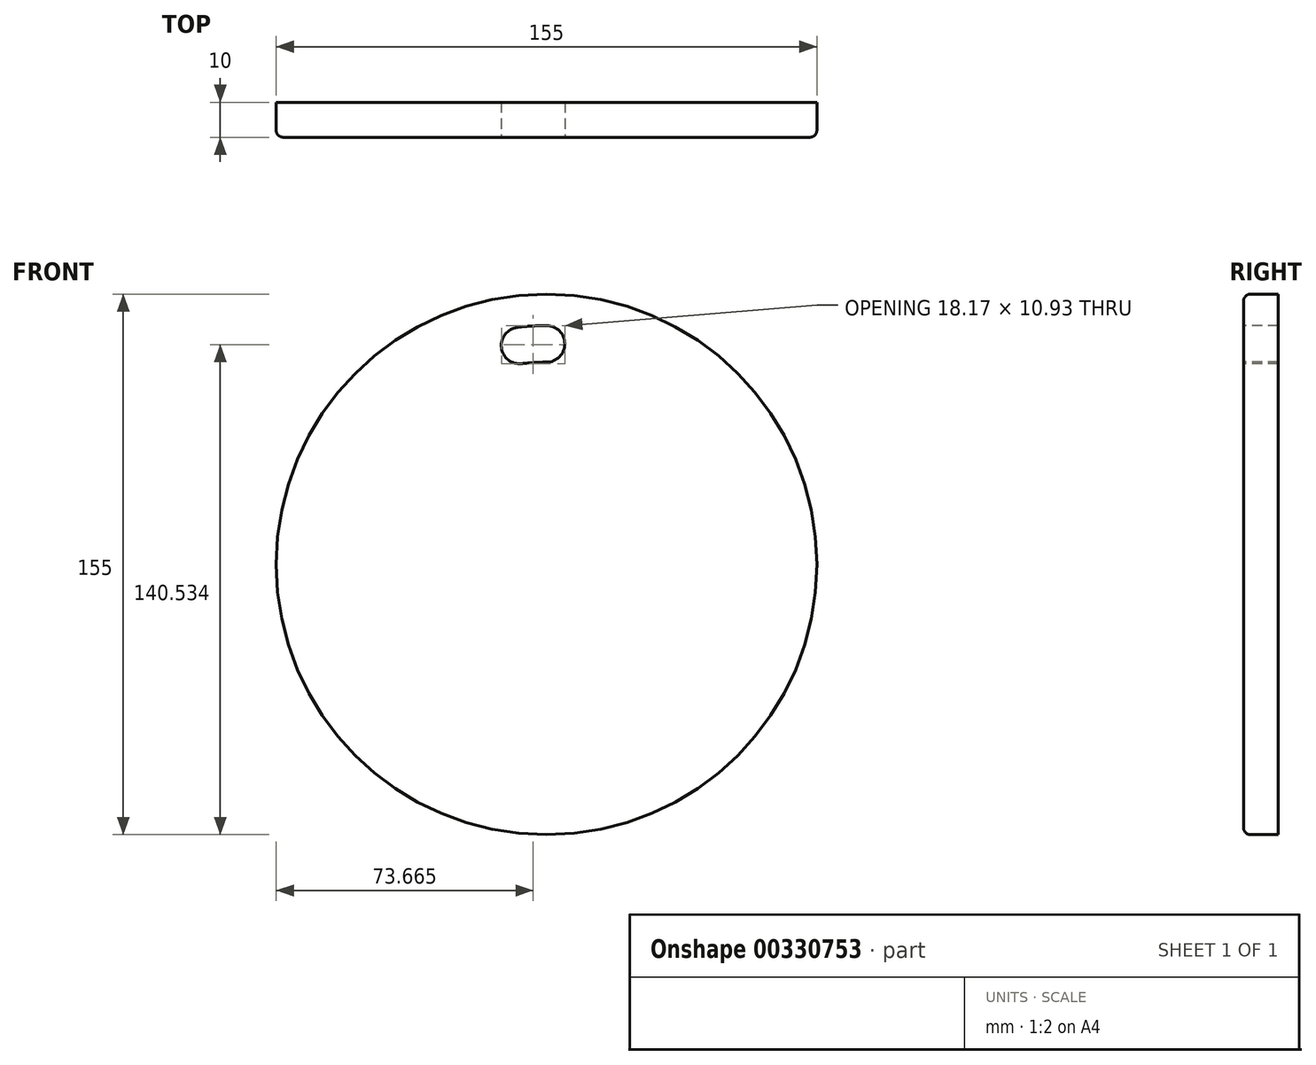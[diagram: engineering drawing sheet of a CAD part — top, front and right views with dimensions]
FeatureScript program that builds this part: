
annotation { "Feature Type Name" : "Feature", "Feature Type Description" : "" }
export const myFeature = defineFeature(function(context is Context, id is Id, definition is map)
    precondition{}
    {
        {
            var Q0;
            Q0=qCreatedBy(makeId("Front.planeOp"),FACE);
            var sketch = newSketch(context, id + "F0", { "sketchPlane" : qUnion([Q0])});
            skCircle(sketch, "E0", {"center": v(0, 0) * mm, "radius": 58 * mm, "construction": true});
            skCircle(sketch, "E1", {"center": v(0, 0) * mm, "radius": 68.5 * mm, "construction": true});
            skLineSegment(sketch, "E2", {"start": v(0, 63.25) * mm, "end": v(0, 58) * mm, "construction": true});
            skLineSegment(sketch, "E3", {"start": v(0, 68.5) * mm, "end": v(0, 63.25) * mm, "construction": true});
            skCircle(sketch, "E4", {"center": v(0, 0) * mm, "radius": 63.25 * mm, "construction": true});
            skLineSegment(sketch, "E5", {"start": v(0, 0) * mm, "end": v(0, 63.25) * mm, "construction": true});
            skLineSegment(sketch, "E6", {"start": v(0, 0) * mm, "end": v(-7.7, 62.78) * mm, "construction": true});
            skArc(sketch, "E7", {"start": v(-8.35, 67.99) * mm, "mid": v(-12.92, 62.14) * mm, "end": v(-7.07, 57.57) * mm});
            skArc(sketch, "E8", {"start": v(0, 58) * mm, "mid": v(5.25, 63.25) * mm, "end": v(0, 68.5) * mm});
            skPoint(sketch, "E9.third.point", {"position": v(-8.35, 67.99) * mm});
            skArc(sketch, "E10", {"start": v(0, 68.5) * mm, "mid": v(-4.18, 68.37) * mm, "end": v(-8.35, 67.99) * mm});
            skArc(sketch, "E11", {"start": v(0, 58) * mm, "mid": v(-3.54, 57.9) * mm, "end": v(-7.07, 57.57) * mm});
            skSolve(sketch);
        }
        {
            var Q0;
            Q0=qCreatedBy(makeId("Front.planeOp"),FACE);
            var sketch = newSketch(context, id + "F1", { "sketchPlane" : qUnion([Q0])});
            skCircle(sketch, "E12", {"center": v(0, 0) * mm, "radius": 77.5 * mm});
            skSolve(sketch);
        }
        {
            var Q0;
            Q0 = qSketchRegion(id + "F1", true);
            extrude(context, id + "F2", {"entities" : qUnion([Q0]), "oppositeDirection" : true, "depth" : 10 * mm});
        }
        {
            var Q0;
            Q0=makeQuery(id+"F2.opExtrude","CAP_EDGE",EDGE,{"disambiguationData":[OSD([sQuery(id+"F1.wireOp",EDGE,"E12")])],"isStart":true});
            fillet(context, id + "F3", {"entities" : qUnion([Q0]), "radius" : 2 * mm, "tangentPropagation" : true, "allowEdgeOverflow" : false});
        }
        {
            var Q0;
            Q0 = qSketchRegion(id + "F0", true);
            var Q1;
            Q1=makeQuery(id+"F2.opExtrude","CAP_FACE",FACE,{"disambiguationData":[OSD([sQuery(id+"F1.wireOp",EDGE,"E12")])],"isStart":false});
            extrude(context, id + "F4", {"entities" : qUnion([Q0]), "operationType" : NewBodyOperationType.REMOVE, "endBound" : BoundingType.UP_TO_SURFACE, "oppositeDirection" : true, "endBoundEntityFace" : qUnion([Q1]), "depth" : 25 * mm});
        }
    });
